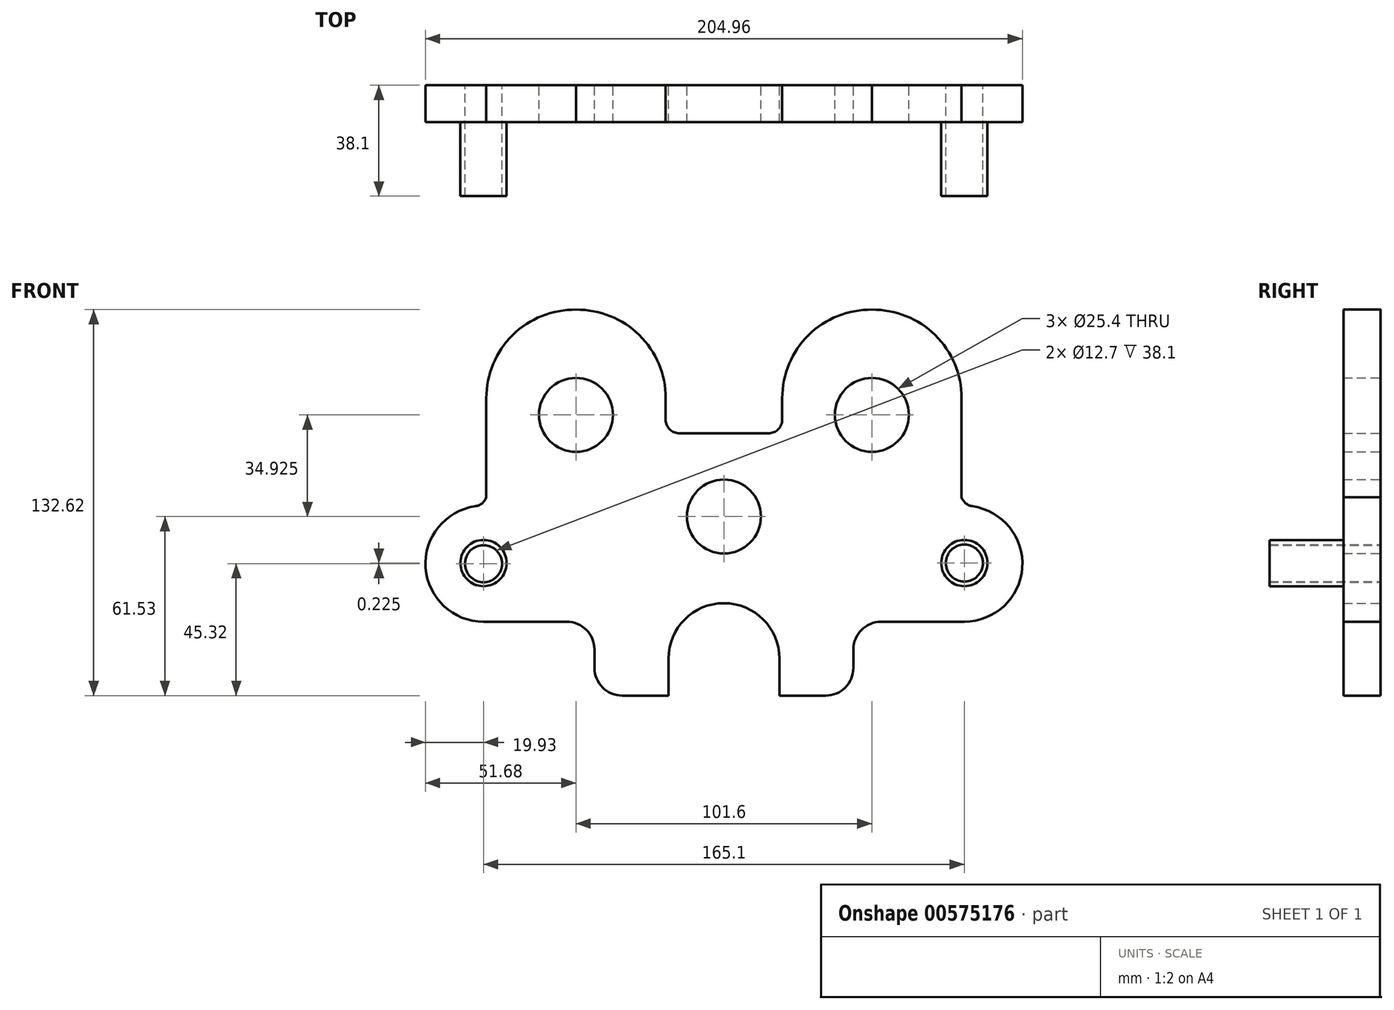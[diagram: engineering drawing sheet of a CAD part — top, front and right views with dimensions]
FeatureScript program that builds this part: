
annotation { "Feature Type Name" : "Feature", "Feature Type Description" : "" }
export const myFeature = defineFeature(function(context is Context, id is Id, definition is map)
    precondition{}
    {
        {
            var Q0;
            Q0=qCreatedBy(makeId("Front.planeOp"),FACE);
            var sketch = newSketch(context, id + "F0", { "sketchPlane" : qUnion([Q0])});
            skCircle(sketch, "E0", {"center": v(0, 0) * mm, "radius": 12.7 * mm});
            skCircle(sketch, "E1", {"center": v(-50.8, 34.92) * mm, "radius": 12.7 * mm});
            skCircle(sketch, "E2", {"center": v(50.8, 34.93) * mm, "radius": 12.7 * mm});
            skCircle(sketch, "E3", {"center": v(-82.55, -16.21) * mm, "radius": 6.35 * mm});
            skCircle(sketch, "E4", {"center": v(82.55, -15.99) * mm, "radius": 6.35 * mm});
            skLineSegment(sketch, "E5", {"start": v(-50.8, 34.92) * mm, "end": v(-50.8, 71.09) * mm, "construction": true});
            skLineSegment(sketch, "E6", {"start": v(50.8, 34.93) * mm, "end": v(104.97, 34.93) * mm, "construction": true});
            skPoint(sketch, "E7", {"position": v(77.89, 34.93) * mm});
            skLineSegment(sketch, "E8", {"start": v(-82.55, -16.21) * mm, "end": v(-82.55, 0) * mm, "construction": true});
            skArc(sketch, "E9", {"start": v(-85.38, 3.52) * mm, "mid": v(-102.43, -17.63) * mm, "end": v(-82.55, -36.14) * mm});
            skLineSegment(sketch, "E10", {"start": v(-82.55, -36.14) * mm, "end": v(-82.55, -36.14) * mm});
            skArc(sketch, "E11.MirrorCS", {"start": v(85.38, 3.52) * mm, "mid": v(102.43, -17.63) * mm, "end": v(82.55, -36.14) * mm});
            skLineSegment(sketch, "E12.MirrorCS", {"start": v(82.55, -36.14) * mm, "end": v(82.55, -36.14) * mm});
            skLineSegment(sketch, "E13", {"start": v(-82.55, -36.14) * mm, "end": v(-53.98, -36.14) * mm});
            skLineSegment(sketch, "E14.MirrorCS", {"start": v(82.55, -36.14) * mm, "end": v(53.98, -36.14) * mm});
            skArc(sketch, "E15", {"start": v(-50.8, 71.09) * mm, "mid": v(-29.05, 62.34) * mm, "end": v(-20, 40.71) * mm});
            skArc(sketch, "E16.MirrorCS", {"start": v(50.8, 71.09) * mm, "mid": v(29.05, 62.34) * mm, "end": v(20, 40.71) * mm});
            skLineSegment(sketch, "E17", {"start": v(-82.55, 3.72) * mm, "end": v(-82.55, 3.72) * mm});
            skLineSegment(sketch, "E18.MirrorCS", {"start": v(82.55, 3.72) * mm, "end": v(82.55, 3.72) * mm});
            skLineSegment(sketch, "E19", {"start": v(-20, 40.71) * mm, "end": v(-20, 33.34) * mm});
            skLineSegment(sketch, "E20.MirrorCS", {"start": v(20, 40.71) * mm, "end": v(20, 33.34) * mm});
            skLineSegment(sketch, "E21", {"start": v(-15.25, 28.58) * mm, "end": v(15.25, 28.58) * mm});
            skLineSegment(sketch, "E22", {"start": v(-34.93, -61.53) * mm, "end": v(-19.05, -61.53) * mm});
            skLineSegment(sketch, "E23", {"start": v(-19.05, -48.83) * mm, "end": v(-19.05, -61.53) * mm});
            skLineSegment(sketch, "E24.MirrorCS", {"start": v(19.05, -48.83) * mm, "end": v(19.05, -61.53) * mm});
            skLineSegment(sketch, "E25.MirrorCS", {"start": v(34.93, -61.53) * mm, "end": v(19.05, -61.53) * mm});
            skArc(sketch, "E26", {"start": v(-19.05, -48.83) * mm, "mid": v(-13.47, -35.36) * mm, "end": v(0, -29.78) * mm});
            skArc(sketch, "E27.MirrorCS", {"start": v(19.05, -48.83) * mm, "mid": v(13.47, -35.36) * mm, "end": v(0, -29.78) * mm});
            skLineSegment(sketch, "E28", {"start": v(-44.45, -44.96) * mm, "end": v(-44.45, -45.67) * mm});
            skLineSegment(sketch, "E29", {"start": v(-44.45, -44.96) * mm, "end": v(-44.45, -52) * mm});
            skLineSegment(sketch, "E30.MirrorCS", {"start": v(44.45, -44.96) * mm, "end": v(44.45, -45.67) * mm});
            skLineSegment(sketch, "E31.MirrorCS", {"start": v(44.45, -44.96) * mm, "end": v(44.45, -52) * mm});
            skPoint(sketch, "E32.visualSharp", {"position": v(-20, 28.57) * mm});
            skArc(sketch, "E32.filletArc", {"start": v(-20, 33.34) * mm, "mid": v(-18.61, 29.97) * mm, "end": v(-15.25, 28.57) * mm});
            skPoint(sketch, "E33.visualSharp", {"position": v(20, 28.57) * mm});
            skArc(sketch, "E33.filletArc", {"start": v(15.25, 28.57) * mm, "mid": v(18.61, 29.97) * mm, "end": v(20, 33.34) * mm});
            skPoint(sketch, "E34.visualSharp", {"position": v(-82.55, 3.72) * mm});
            skArc(sketch, "E34.filletArc", {"start": v(-85.38, 3.52) * mm, "mid": v(-83.07, 4.53) * mm, "end": v(-81.6, 6.58) * mm});
            skPoint(sketch, "E35.visualSharp", {"position": v(82.55, 3.72) * mm});
            skArc(sketch, "E35.filletArc", {"start": v(81.6, 6.57) * mm, "mid": v(83.07, 4.52) * mm, "end": v(85.38, 3.52) * mm});
            skPoint(sketch, "E36.visualSharp", {"position": v(-44.45, -61.53) * mm});
            skArc(sketch, "E36.filletArc", {"start": v(-44.45, -52) * mm, "mid": v(-41.66, -58.74) * mm, "end": v(-34.93, -61.53) * mm});
            skPoint(sketch, "E37.visualSharp", {"position": v(44.45, -61.53) * mm});
            skArc(sketch, "E37.filletArc", {"start": v(34.93, -61.53) * mm, "mid": v(41.66, -58.74) * mm, "end": v(44.45, -52) * mm});
            skPoint(sketch, "E38.visualSharp", {"position": v(-44.45, -36.14) * mm});
            skArc(sketch, "E38.filletArc", {"start": v(-44.45, -45.67) * mm, "mid": v(-47.24, -38.93) * mm, "end": v(-53.98, -36.14) * mm});
            skPoint(sketch, "E39.visualSharp", {"position": v(44.45, -36.14) * mm});
            skArc(sketch, "E39.filletArc", {"start": v(53.98, -36.14) * mm, "mid": v(47.24, -38.93) * mm, "end": v(44.45, -45.67) * mm});
            skArc(sketch, "E40.MirrorCS", {"start": v(-50.8, 71.09) * mm, "mid": v(-72.55, 62.34) * mm, "end": v(-81.6, 40.71) * mm});
            skLineSegment(sketch, "E41", {"start": v(-81.6, 40.71) * mm, "end": v(-81.6, 6.58) * mm});
            skArc(sketch, "E42.MirrorCS", {"start": v(50.8, 71.09) * mm, "mid": v(72.55, 62.34) * mm, "end": v(81.6, 40.71) * mm});
            skLineSegment(sketch, "E43", {"start": v(81.6, 40.71) * mm, "end": v(81.6, 6.57) * mm});
            skCircle(sketch, "E44", {"center": v(82.55, -15.99) * mm, "radius": 7.94 * mm});
            skCircle(sketch, "E45", {"center": v(-82.55, -15.99) * mm, "radius": 7.94 * mm});
            skSolve(sketch);
        }
        {
            var Q0;
            Q0 = qSketchRegion(id + "F0", true);
            var Q1;
            Q1=makeQuery(id+"F0.imprint","IMPRINT",FACE,{"disambiguationData":[TD([[makeQuery(id+"F0.imprint","IMPRINT",EDGE,{"derivedFrom":sQuery(id+"F0.wireOp",EDGE,"E3")}),-1.0]])]});
            var Q2;
            Q2=makeQuery(id+"F0.imprint","IMPRINT",FACE,{"disambiguationData":[TD([[makeQuery(id+"F0.imprint","IMPRINT",EDGE,{"derivedFrom":sQuery(id+"F0.wireOp",EDGE,"E4")}),-1.0]])]});
            extrude(context, id + "F1", {"entities" : qUnion([Q0, Q1, Q2]), "depth" : 12.7 * mm, "offsetDistance" : 25.4 * mm});
        }
        {
            var Q0;
            Q0=makeQuery(id+"F0.imprint","IMPRINT",FACE,{"disambiguationData":[TD([[makeQuery(id+"F0.imprint","IMPRINT",EDGE,{"derivedFrom":sQuery(id+"F0.wireOp",EDGE,"E4")}),-1.0]])]});
            var Q1;
            Q1=makeQuery(id+"F0.imprint","IMPRINT",FACE,{"disambiguationData":[TD([[makeQuery(id+"F0.imprint","IMPRINT",EDGE,{"derivedFrom":sQuery(id+"F0.wireOp",EDGE,"E3")}),-1.0]])]});
            extrude(context, id + "F2", {"entities" : qUnion([Q0, Q1]), "operationType" : NewBodyOperationType.ADD, "depth" : 38.1 * mm, "offsetDistance" : 25.4 * mm});
        }
    });
